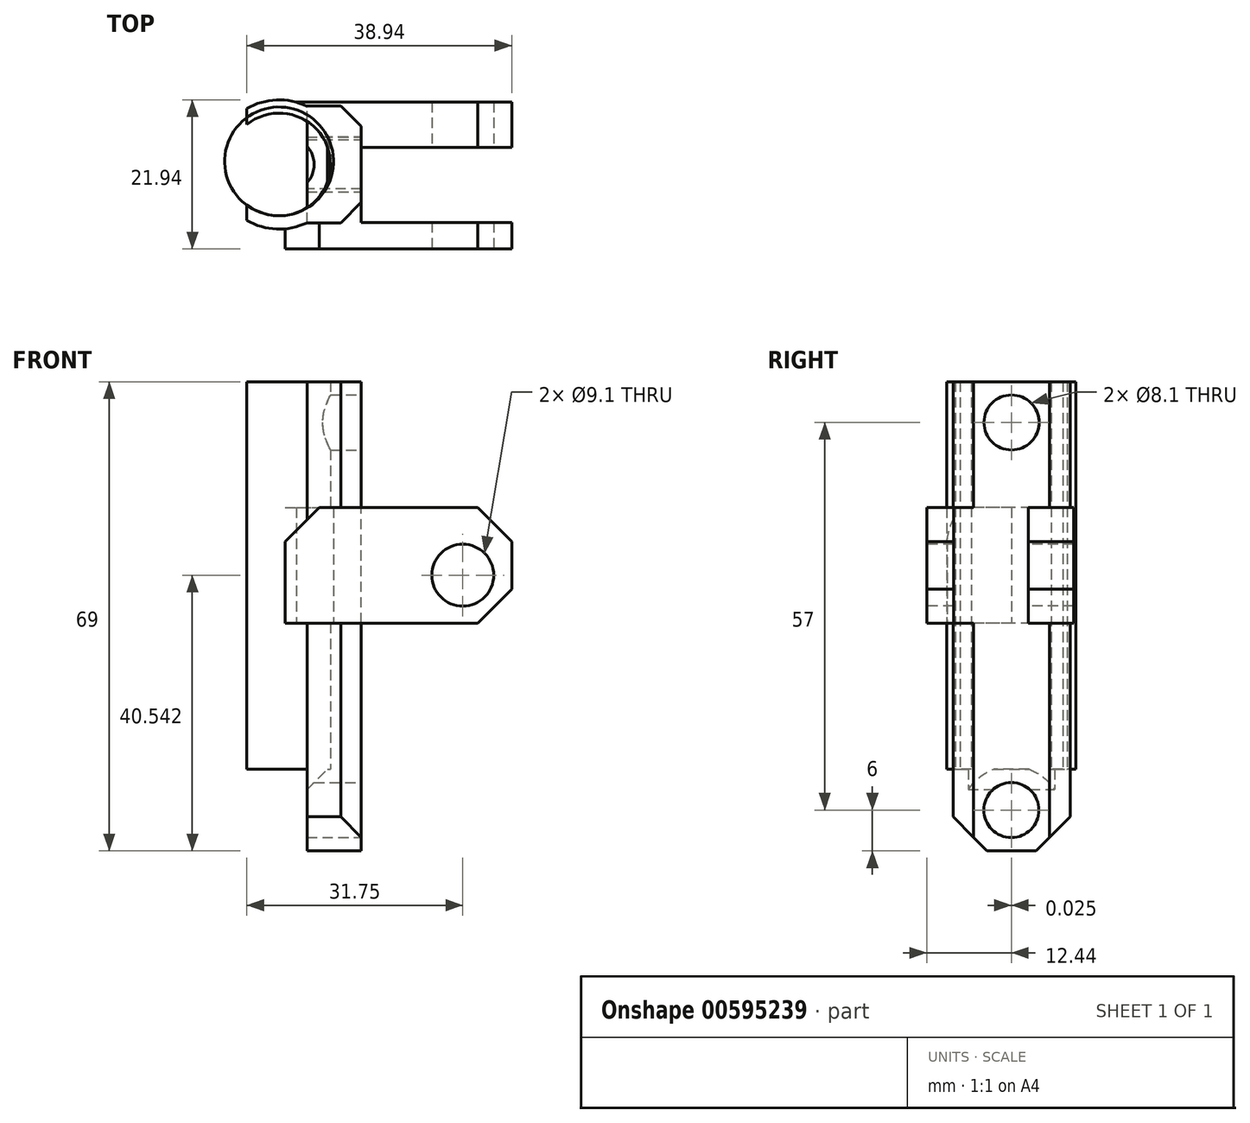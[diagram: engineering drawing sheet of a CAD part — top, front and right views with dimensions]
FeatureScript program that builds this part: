
annotation { "Feature Type Name" : "Feature", "Feature Type Description" : "" }
export const myFeature = defineFeature(function(context is Context, id is Id, definition is map)
    precondition{}
    {
        {
            var Q0;
            Q0=qCreatedBy(makeId("Top.planeOp"),FACE);
            var sketch = newSketch(context, id + "F0", { "sketchPlane" : qUnion([Q0])});
            skCircle(sketch, "E0", {"center": v(0, 0) * mm, "radius": 7.55 * mm});
            skCircle(sketch, "E1", {"center": v(0, 0) * mm, "radius": 9.5 * mm});
            skLineSegment(sketch, "E2", {"start": v(0, 0) * mm, "end": v(-9.5, 0) * mm});
            skLineSegment(sketch, "E3", {"start": v(-9.5, 0) * mm, "end": v(-4.75, 0) * mm});
            skLineSegment(sketch, "E4", {"start": v(-4.75, 0) * mm, "end": v(-4.75, -10.14) * mm});
            skLineSegment(sketch, "E5", {"start": v(-4.75, -10.14) * mm, "end": v(-4.75, 9.64) * mm});
            skCircle(sketch, "E6", {"center": v(0, 0) * mm, "radius": 4.05 * mm});
            skSolve(sketch);
        }
        {
            var Q0;
            {var subQ0=sQuery(id+"F0.wireOp",EDGE,"E5");var subQ1=sQuery(id+"F0.wireOp",EDGE,"E0");var subQ2=makeQuery(id+"F0.imprint","INTERSECT",VERTEX,{"disambiguationData":[OD(0.0)],"derivedFrom":[subQ1,subQ0]});Q0=makeQuery(id+"F0.imprint","IMPRINT",FACE,{"disambiguationData":[TD([[makeQuery(id+"F0.imprint","IMPRINT",EDGE,{"disambiguationData":[TD([[subQ2,1.0]])],"derivedFrom":subQ1}),-1.0]])]});}
            extrude(context, id + "F1", {"entities" : qUnion([Q0]), "depth" : 45 * mm, "offsetDistance" : 25 * mm});
        }
        {
            var Q0;
            Q0=makeQuery(id+"F0.imprint","IMPRINT",FACE,{"disambiguationData":[TD([[makeQuery(id+"F0.imprint","IMPRINT",EDGE,{"derivedFrom":sQuery(id+"F0.wireOp",EDGE,"E6")}),1.0]])]});
            extrude(context, id + "F2", {"entities" : qUnion([Q0]), "depth" : 102.3 * mm, "offsetDistance" : 25 * mm});
        }
        {
            var Q0;
            Q0=makeQuery(id+"F0.imprint","IMPRINT",FACE,{"disambiguationData":[TD([[makeQuery(id+"F0.imprint","IMPRINT",EDGE,{"derivedFrom":sQuery(id+"F0.wireOp",EDGE,"E6")}),1.0]])]});
            extrude(context, id + "F3", {"entities" : qUnion([Q0]), "operationType" : NewBodyOperationType.ADD, "depth" : 25 * mm, "offsetDistance" : 25 * mm});
        }
        {
            var Q0;
            Q0=makeQuery(id+"F0.imprint","IMPRINT",FACE,{"disambiguationData":[TD([[makeQuery(id+"F0.imprint","IMPRINT",EDGE,{"derivedFrom":sQuery(id+"F0.wireOp",EDGE,"E6")}),1.0]])]});
            extrude(context, id + "F4", {"entities" : qUnion([Q0]), "operationType" : NewBodyOperationType.ADD, "oppositeDirection" : true, "depth" : 24.6 * mm, "offsetDistance" : 25 * mm});
        }
        {
            var Q0;
            Q0=makeQuery(id+"F1.opExtrude","CAP_FACE",FACE,{"disambiguationData":[OSD([sQuery(id+"F0.wireOp",EDGE,"E0"),sQuery(id+"F0.wireOp",EDGE,"E1"),sQuery(id+"F0.wireOp",EDGE,"E5")])],"isStart":false});
            var sketch = newSketch(context, id + "F5", { "sketchPlane" : qUnion([Q0])});
            skLineSegment(sketch, "E7", {"start": v(4.09, 0) * mm, "end": v(4.09, -8.58) * mm});
            skLineSegment(sketch, "E8.bottom", {"start": v(4.09, -8.58) * mm, "end": v(12.09, -8.58) * mm});
            skLineSegment(sketch, "E8.top", {"start": v(4.09, 8.62) * mm, "end": v(12.09, 8.62) * mm});
            skLineSegment(sketch, "E8.left", {"start": v(4.09, -8.58) * mm, "end": v(4.09, 8.62) * mm});
            skLineSegment(sketch, "E8.right", {"start": v(12.09, -8.58) * mm, "end": v(12.09, 8.62) * mm});
            skSolve(sketch);
        }
        {
            var Q0;
            {var subQ4=sQuery(id+"F5.wireOp",EDGE,"E8.bottom");Q0=makeQuery(id+"F5.imprint","IMPRINT",FACE,{"disambiguationData":[TD([[makeQuery(id+"F5.imprint","IMPRINT",EDGE,{"derivedFrom":subQ4}),1.0]])]});}
            var Q1;
            {var subQ0=sQuery(id+"F5.wireOp",EDGE,"E8.left");var subQ3=makeQuery(id+"F1.opExtrude","CAP_EDGE",EDGE,{"disambiguationData":[OSD([sQuery(id+"F0.wireOp",EDGE,"E0")])],"isStart":false});var subQ5=makeQuery(id+"F5.imprint","INTERSECT",VERTEX,{"disambiguationData":[OD(1.0)],"derivedFrom":[subQ3,subQ0]});Q1=makeQuery(id+"F5.imprint","IMPRINT",FACE,{"disambiguationData":[TD([[makeQuery(id+"F5.imprint","IMPRINT",EDGE,{"disambiguationData":[TD([[subQ5,-1.0]])],"derivedFrom":subQ0}),-1.0]])]});}
            var Q2;
            {var subQ0=sQuery(id+"F5.wireOp",EDGE,"E8.left");var subQ1=makeQuery(id+"F1.opExtrude","CAP_EDGE",EDGE,{"disambiguationData":[OSD([sQuery(id+"F0.wireOp",EDGE,"E0")])],"isStart":false});var subQ2=makeQuery(id+"F5.imprint","INTERSECT",VERTEX,{"disambiguationData":[OD(0.0)],"derivedFrom":[subQ1,subQ0]});Q2=makeQuery(id+"F5.imprint","IMPRINT",FACE,{"disambiguationData":[TD([[makeQuery(id+"F5.imprint","IMPRINT",EDGE,{"disambiguationData":[TD([[subQ2,-1.0]])],"derivedFrom":subQ0}),-1.0]])]});}
            extrude(context, id + "F6", {"entities" : qUnion([Q0, Q1, Q2]), "operationType" : NewBodyOperationType.ADD, "depth" : 12 * mm, "offsetDistance" : 25 * mm});
        }
        {
            var Q0;
            Q0=makeQuery(id+"F6.opExtrude","SWEPT_FACE",FACE,{"disambiguationData":[OSD([sQuery(id+"F5.wireOp",EDGE,"E8.right")])]});
            var sketch = newSketch(context, id + "F7", { "sketchPlane" : qUnion([Q0])});
            skCircle(sketch, "E9", {"center": v(0.02, 51) * mm, "radius": 4.05 * mm});
            skPoint(sketch, "E9.centerSnap0", {"position": v(-8.58, 51) * mm});
            skPoint(sketch, "E9.centerSnap1", {"position": v(0.02, 57) * mm});
            skSolve(sketch);
        }
        {
            var Q0;
            Q0=makeQuery(id+"F7.imprint","IMPRINT",FACE,{"disambiguationData":[TD([[makeQuery(id+"F7.imprint","IMPRINT",EDGE,{"derivedFrom":sQuery(id+"F7.wireOp",EDGE,"E9")}),1.0]])]});
            extrude(context, id + "F8", {"entities" : qUnion([Q0]), "operationType" : NewBodyOperationType.REMOVE, "oppositeDirection" : true, "depth" : 25 * mm, "offsetDistance" : 25 * mm});
        }
        {
            var Q0;
            {var subQ0=sQuery(id+"F5.wireOp",EDGE,"E8.bottom");var subQ1=sQuery(id+"F5.wireOp",EDGE,"E8.top");var subQ2=sQuery(id+"F0.wireOp",EDGE,"E1");var subQ3=sQuery(id+"F5.wireOp",EDGE,"E8.left");var subQ4=sQuery(id+"F5.wireOp",EDGE,"E8.right");Q0=makeQuery(id+"F6.boolean.opBoolean","SPLIT",FACE,{"disambiguationData":[TD([makeQuery(id+"F1.opExtrude","SWEPT_FACE",FACE,{"disambiguationData":[OSD([subQ2])]})])],"derivedFrom":makeQuery(id+"F6.opExtrude","CAP_FACE",FACE,{"disambiguationData":[OSD([subQ0,subQ1,subQ3,subQ4])],"isStart":true})});}
            extrude(context, id + "F9", {"entities" : qUnion([Q0]), "operationType" : NewBodyOperationType.ADD, "depth" : 45 * mm, "offsetDistance" : 25 * mm});
        }
        {
            var Q0;
            Q0=makeQuery(id+"F9.boolean.opBoolean","MERGE",FACE,{"derivedFrom":[makeQuery(id+"F1.opExtrude","CAP_FACE",FACE,{"disambiguationData":[OSD([sQuery(id+"F0.wireOp",EDGE,"E0"),sQuery(id+"F0.wireOp",EDGE,"E1"),sQuery(id+"F0.wireOp",EDGE,"E5")])],"isStart":true}),makeQuery(id+"F9.opExtrude","CAP_FACE",FACE,{"disambiguationData":[OSD([sQuery(id+"F5.wireOp",EDGE,"E8.bottom"),sQuery(id+"F5.wireOp",EDGE,"E8.top"),sQuery(id+"F5.wireOp",EDGE,"E8.left"),sQuery(id+"F5.wireOp",EDGE,"E8.right")])],"isStart":false})]});
            var sketch = newSketch(context, id + "F10", { "sketchPlane" : qUnion([Q0])});
            skLineSegment(sketch, "E10.bottom", {"start": v(12.09, 8.58) * mm, "end": v(4.09, 8.58) * mm});
            skLineSegment(sketch, "E10.top", {"start": v(12.09, -8.62) * mm, "end": v(4.09, -8.62) * mm});
            skLineSegment(sketch, "E10.left", {"start": v(12.09, 8.58) * mm, "end": v(12.09, -8.62) * mm});
            skLineSegment(sketch, "E10.right", {"start": v(4.09, 8.58) * mm, "end": v(4.09, -8.62) * mm});
            skSolve(sketch);
        }
        {
            var Q0;
            {var subQ1=sQuery(id+"F10.wireOp",EDGE,"E10.bottom");Q0=makeQuery(id+"F10.imprint","IMPRINT",FACE,{"disambiguationData":[TD([[makeQuery(id+"F10.imprint","IMPRINT",EDGE,{"derivedFrom":subQ1}),-1.0]])]});}
            var Q1;
            {var subQ0=sQuery(id+"F10.wireOp",EDGE,"E10.right");var subQ1=makeQuery(id+"F1.opExtrude","CAP_EDGE",EDGE,{"disambiguationData":[OSD([sQuery(id+"F0.wireOp",EDGE,"E0")])],"isStart":true});var subQ2=makeQuery(id+"F10.imprint","INTERSECT",VERTEX,{"disambiguationData":[OD(0.0)],"derivedFrom":[subQ1,subQ0]});Q1=makeQuery(id+"F10.imprint","IMPRINT",FACE,{"disambiguationData":[TD([[makeQuery(id+"F10.imprint","IMPRINT",EDGE,{"disambiguationData":[TD([[subQ2,-1.0]])],"derivedFrom":subQ0}),1.0]])]});}
            extrude(context, id + "F11", {"entities" : qUnion([Q0, Q1]), "operationType" : NewBodyOperationType.ADD, "depth" : 12 * mm, "offsetDistance" : 25 * mm});
        }
        {
            var Q0;
            {var subQ0=sQuery(id+"F5.wireOp",EDGE,"E8.right");Q0=makeQuery(id+"F11.boolean.opBoolean","MERGE",FACE,{"derivedFrom":[makeQuery(id+"F9.boolean.opBoolean","MERGE",FACE,{"derivedFrom":[makeQuery(id+"F6.opExtrude","SWEPT_FACE",FACE,{"disambiguationData":[OSD([subQ0])]}),makeQuery(id+"F9.opExtrude","SWEPT_FACE",FACE,{"disambiguationData":[OSD([subQ0])]})]}),makeQuery(id+"F11.opExtrude","SWEPT_FACE",FACE,{"disambiguationData":[OSD([sQuery(id+"F10.wireOp",EDGE,"E10.left")])]})]});}
            var sketch = newSketch(context, id + "F12", { "sketchPlane" : qUnion([Q0])});
            skLineSegment(sketch, "E11", {"start": v(-8.58, -12) * mm, "end": v(-8.58, 0) * mm});
            skLineSegment(sketch, "E12", {"start": v(-8.58, 0) * mm, "end": v(8.62, 0) * mm});
            skCircle(sketch, "E13", {"center": v(0, -6) * mm, "radius": 4.05 * mm});
            skPoint(sketch, "E13.centerSnap0", {"position": v(-8.58, -6) * mm});
            skSolve(sketch);
        }
        {
            var Q0;
            Q0=makeQuery(id+"F12.imprint","IMPRINT",FACE,{"disambiguationData":[TD([[makeQuery(id+"F12.imprint","IMPRINT",EDGE,{"derivedFrom":sQuery(id+"F12.wireOp",EDGE,"E13")}),1.0]])]});
            extrude(context, id + "F13", {"entities" : qUnion([Q0]), "operationType" : NewBodyOperationType.REMOVE, "oppositeDirection" : true, "depth" : 25 * mm, "offsetDistance" : 25 * mm});
        }
        {
            var Q0;
            {var subQ0=sQuery(id+"F0.wireOp",EDGE,"E5");var subQ1=sQuery(id+"F0.wireOp",EDGE,"E1");var subQ2=sQuery(id+"F0.wireOp",EDGE,"E0");var subQ3=sQuery(id+"F5.wireOp",EDGE,"E8.bottom");Q0=makeQuery(id+"F6.boolean.opBoolean","SPLIT",FACE,{"disambiguationData":[TD([makeQuery(id+"F6.opExtrude","SWEPT_FACE",FACE,{"disambiguationData":[OSD([subQ3])]})])],"derivedFrom":makeQuery(id+"F1.opExtrude","CAP_FACE",FACE,{"disambiguationData":[OSD([subQ2,subQ1,subQ0])],"isStart":false})});}
            var Q1;
            {var subQ1=sQuery(id+"F0.wireOp",EDGE,"E1");var subQ2=sQuery(id+"F0.wireOp",EDGE,"E5");var subQ3=sQuery(id+"F0.wireOp",EDGE,"E0");Q1=makeQuery(id+"F6.boolean.opBoolean","SPLIT",FACE,{"disambiguationData":[TD([makeQuery(id+"F1.opExtrude","SWEPT_FACE",FACE,{"disambiguationData":[OSD([subQ2]),TDD([makeQuery(id+"F0.imprint","IMPRINT",EDGE,{"disambiguationData":[TD([[makeQuery(id+"F0.imprint","INTERSECT",VERTEX,{"disambiguationData":[OD(0.0)],"derivedFrom":[subQ1,subQ2]}),1.0]])],"derivedFrom":subQ2})])]})])],"derivedFrom":makeQuery(id+"F1.opExtrude","CAP_FACE",FACE,{"disambiguationData":[OSD([subQ3,subQ1,subQ2])],"isStart":false})});}
            extrude(context, id + "F14", {"entities" : qUnion([Q0, Q1]), "operationType" : NewBodyOperationType.ADD, "depth" : 12 * mm, "offsetDistance" : 25 * mm});
        }
        {
            var Q0;
            Q0=makeQuery(id+"F11.opExtrude","CAP_EDGE",EDGE,{"disambiguationData":[OSD([sQuery(id+"F10.wireOp",EDGE,"E10.top")])],"isStart":false});
            var Q1;
            Q1=makeQuery(id+"F11.opExtrude","CAP_EDGE",EDGE,{"disambiguationData":[OSD([sQuery(id+"F10.wireOp",EDGE,"E10.bottom")])],"isStart":false});
            chamfer(context, id + "F15", {"entities" : qUnion([Q0, Q1]), "width" : 5 * mm, "tangentPropagation" : true});
        }
        {
            var Q0;
            {var subQ0=sQuery(id+"F5.wireOp",EDGE,"E8.right");var subQ1=sQuery(id+"F5.wireOp",EDGE,"E8.top");Q0=makeQuery(id+"F11.boolean.opBoolean","MERGE",EDGE,{"derivedFrom":[makeQuery(id+"F9.boolean.opBoolean","MERGE",EDGE,{"derivedFrom":[makeQuery(id+"F6.opExtrude","SWEPT_EDGE",EDGE,{"disambiguationData":[OSD([subQ1,subQ0])]}),makeQuery(id+"F9.opExtrude","SWEPT_EDGE",EDGE,{"disambiguationData":[OSD([subQ1,subQ0])]})]}),makeQuery(id+"F11.opExtrude","SWEPT_EDGE",EDGE,{"disambiguationData":[OSD([sQuery(id+"F10.wireOp",EDGE,"E10.top"),sQuery(id+"F10.wireOp",EDGE,"E10.left")])]})]});}
            var Q1;
            {var subQ0=sQuery(id+"F5.wireOp",EDGE,"E8.right");var subQ1=sQuery(id+"F5.wireOp",EDGE,"E8.bottom");Q1=makeQuery(id+"F11.boolean.opBoolean","MERGE",EDGE,{"derivedFrom":[makeQuery(id+"F9.boolean.opBoolean","MERGE",EDGE,{"derivedFrom":[makeQuery(id+"F6.opExtrude","SWEPT_EDGE",EDGE,{"disambiguationData":[OSD([subQ1,subQ0])]}),makeQuery(id+"F9.opExtrude","SWEPT_EDGE",EDGE,{"disambiguationData":[OSD([subQ1,subQ0])]})]}),makeQuery(id+"F11.opExtrude","SWEPT_EDGE",EDGE,{"disambiguationData":[OSD([sQuery(id+"F10.wireOp",EDGE,"E10.bottom"),sQuery(id+"F10.wireOp",EDGE,"E10.left")])]})]});}
            chamfer(context, id + "F16", {"entities" : qUnion([Q0, Q1]), "width" : 3 * mm, "tangentPropagation" : true});
        }
        {
            var Q0;
            Q0=makeQuery(id+"F4.opExtrude","CAP_FACE",FACE,{"disambiguationData":[OSD([sQuery(id+"F0.wireOp",EDGE,"E6")])],"isStart":false});
            extrude(context, id + "F17", {"entities" : qUnion([Q0]), "operationType" : NewBodyOperationType.REMOVE, "oppositeDirection" : true, "depth" : 164 * mm, "offsetDistance" : 25 * mm});
        }
        {
            var Q0;
            {var subQ0=sQuery(id+"F5.wireOp",EDGE,"E8.left");var subQ1=sQuery(id+"F10.wireOp",EDGE,"E10.right");Q0=makeQuery(id+"F11.boolean.opBoolean","SPLIT",EDGE,{"disambiguationData":[topologyDisambiguationEdgeConnected([makeQuery(id+"F6.opExtrude","SWEPT_FACE",FACE,{"disambiguationData":[OSD([subQ0])]}),makeQuery(id+"F9.opExtrude","SWEPT_FACE",FACE,{"disambiguationData":[OSD([subQ0])]}),makeQuery(id+"F11.opExtrude","CAP_FACE",FACE,{"disambiguationData":[OSD([sQuery(id+"F10.wireOp",EDGE,"E10.bottom"),sQuery(id+"F10.wireOp",EDGE,"E10.top"),sQuery(id+"F10.wireOp",EDGE,"E10.left"),subQ1])],"isStart":true}),makeQuery(id+"F11.opExtrude","SWEPT_FACE",FACE,{"disambiguationData":[OSD([subQ1])]})])],"derivedFrom":makeQuery(id+"F11.opExtrude","CAP_EDGE",EDGE,{"disambiguationData":[OSD([subQ1])],"isStart":true})});}
            chamfer(context, id + "F18", {"entities" : qUnion([Q0]), "width" : 3 * mm, "tangentPropagation" : true});
        }
        {
            var Q0;
            {var subQ0=sQuery(id+"F5.wireOp",EDGE,"E8.right");Q0=makeQuery(id+"F11.boolean.opBoolean","MERGE",FACE,{"derivedFrom":[makeQuery(id+"F9.boolean.opBoolean","MERGE",FACE,{"derivedFrom":[makeQuery(id+"F6.opExtrude","SWEPT_FACE",FACE,{"disambiguationData":[OSD([subQ0])]}),makeQuery(id+"F9.opExtrude","SWEPT_FACE",FACE,{"disambiguationData":[OSD([subQ0])]})]}),makeQuery(id+"F11.opExtrude","SWEPT_FACE",FACE,{"disambiguationData":[OSD([sQuery(id+"F10.wireOp",EDGE,"E10.left")])]})]});}
            var sketch = newSketch(context, id + "F19", { "sketchPlane" : qUnion([Q0])});
            skLineSegment(sketch, "E14", {"start": v(0, -10.05) * mm, "end": v(0, -1.95) * mm});
            skLineSegment(sketch, "E15", {"start": v(0, -1.95) * mm, "end": v(0, -6) * mm});
            skLineSegment(sketch, "E16", {"start": v(0, -6) * mm, "end": v(-4.87, -6) * mm});
            skLineSegment(sketch, "E17", {"start": v(0, 46.95) * mm, "end": v(0, 55.05) * mm});
            skLineSegment(sketch, "E18", {"start": v(0, 55.05) * mm, "end": v(0.02, 51) * mm});
            skLineSegment(sketch, "E19", {"start": v(0.02, 51) * mm, "end": v(-4.92, 50.97) * mm});
            skLineSegment(sketch, "E20", {"start": v(-2.44, -6) * mm, "end": v(-2.44, 50.98) * mm});
            skLineSegment(sketch, "E21", {"start": v(-2.44, -6) * mm, "end": v(-2.44, 22.5) * mm});
            skLineSegment(sketch, "E22", {"start": v(-2.44, 22.5) * mm, "end": v(-2.44, 15.5) * mm});
            skLineSegment(sketch, "E23.bottom", {"start": v(-2.44, 15.5) * mm, "end": v(-12.44, 15.5) * mm});
            skLineSegment(sketch, "E23.top", {"start": v(-2.44, 22.5) * mm, "end": v(-12.44, 22.5) * mm});
            skLineSegment(sketch, "E23.left", {"start": v(-2.44, 15.5) * mm, "end": v(-2.44, 22.5) * mm});
            skLineSegment(sketch, "E23.right", {"start": v(-12.44, 15.5) * mm, "end": v(-12.44, 22.5) * mm});
            skLineSegment(sketch, "E24", {"start": v(-8.44, 15.5) * mm, "end": v(-8.44, 22.5) * mm});
            skSolve(sketch);
        }
        {
            var Q0;
            {var subQ0=sQuery(id+"F19.wireOp",EDGE,"E23.right");Q0=makeQuery(id+"F19.imprint","IMPRINT",FACE,{"disambiguationData":[TD([[makeQuery(id+"F19.imprint","IMPRINT",EDGE,{"derivedFrom":subQ0}),-1.0]])]});}
            extrude(context, id + "F20", {"entities" : qUnion([Q0]), "operationType" : NewBodyOperationType.ADD, "oppositeDirection" : true, "depth" : 11.2 * mm, "offsetDistance" : 25 * mm});
        }
        {
            var Q0;
            {var subQ0=sQuery(id+"F19.wireOp",EDGE,"E23.right");Q0=makeQuery(id+"F19.imprint","IMPRINT",FACE,{"disambiguationData":[TD([[makeQuery(id+"F19.imprint","IMPRINT",EDGE,{"derivedFrom":subQ0}),-1.0]])]});}
            extrude(context, id + "F21", {"entities" : qUnion([Q0]), "operationType" : NewBodyOperationType.ADD, "depth" : 40 * mm, "offsetDistance" : 25 * mm});
        }
        {
            var Q0;
            {var subQ0=sQuery(id+"F19.wireOp",EDGE,"E23.right");Q0=makeQuery(id+"F21.boolean.opBoolean","MERGE",FACE,{"derivedFrom":[makeQuery(id+"F20.opExtrude","SWEPT_FACE",FACE,{"disambiguationData":[OSD([subQ0])]}),makeQuery(id+"F21.opExtrude","SWEPT_FACE",FACE,{"disambiguationData":[OSD([subQ0])]})]});}
            var sketch = newSketch(context, id + "F22", { "sketchPlane" : qUnion([Q0])});
            skLineSegment(sketch, "E25", {"start": v(4.09, 15.5) * mm, "end": v(-4.75, 15.5) * mm});
            skLineSegment(sketch, "E26", {"start": v(-4.75, 15.5) * mm, "end": v(-0.33, 15.5) * mm});
            skLineSegment(sketch, "E27", {"start": v(2.22, 15.5) * mm, "end": v(2.22, 22.5) * mm});
            skLineSegment(sketch, "E28", {"start": v(2.22, 22.5) * mm, "end": v(2.22, 19) * mm});
            skLineSegment(sketch, "E29", {"start": v(0, 19) * mm, "end": v(27, 19) * mm});
            skCircle(sketch, "E30", {"center": v(27, 28.54) * mm, "radius": 4.55 * mm});
            skSolve(sketch);
        }
        {
            var Q0;
            {var subQ0=sQuery(id+"F19.wireOp",EDGE,"E23.top");Q0=makeQuery(id+"F21.boolean.opBoolean","MERGE",FACE,{"derivedFrom":[makeQuery(id+"F20.opExtrude","SWEPT_FACE",FACE,{"disambiguationData":[OSD([subQ0])]}),makeQuery(id+"F21.opExtrude","SWEPT_FACE",FACE,{"disambiguationData":[OSD([subQ0])]})]});}
            extrude(context, id + "F23", {"entities" : qUnion([Q0]), "operationType" : NewBodyOperationType.ADD, "depth" : 16 * mm, "offsetDistance" : 25 * mm});
        }
        {
            var Q0;
            {var subQ0=sQuery(id+"F19.wireOp",EDGE,"E23.top");var subQ1=sQuery(id+"F19.wireOp",EDGE,"E23.bottom");Q0=makeQuery(id+"F23.boolean.opBoolean","MERGE",FACE,{"derivedFrom":[makeQuery(id+"FqEzdGLLWJqbQr5_1.boolean.opBoolean","MERGE",FACE,{"derivedFrom":[makeQuery(id+"F21.opExtrude","CAP_FACE",FACE,{"disambiguationData":[OSD([subQ1,subQ0,sQuery(id+"F19.wireOp",EDGE,"E23.right"),sQuery(id+"F19.wireOp",EDGE,"E24")])],"isStart":false}),makeQuery(id+"FqEzdGLLWJqbQr5_1.opExtrude","SWEPT_FACE",FACE,{"disambiguationData":[OSD([subQ1]),TDD([makeQuery(id+"F21.opExtrude","CAP_EDGE",EDGE,{"disambiguationData":[OSD([subQ1])],"isStart":false})])]})]}),makeQuery(id+"F23.opExtrude","SWEPT_FACE",FACE,{"disambiguationData":[OSD([subQ0]),TDD([makeQuery(id+"F21.opExtrude","CAP_EDGE",EDGE,{"disambiguationData":[OSD([subQ0])],"isStart":false})])]})]});}
            extrude(context, id + "F24", {"entities" : qUnion([Q0]), "operationType" : NewBodyOperationType.REMOVE, "oppositeDirection" : true, "depth" : 17.9 * mm, "offsetDistance" : 25 * mm});
        }
        {
            var Q0;
            {var subQ0=sQuery(id+"F22.wireOp",EDGE,"E30");var subQ9=makeQuery(id+"F22.imprint","INTERSECT",VERTEX,{"derivedFrom":[sQuery(id+"F22.wireOp",EDGE,"E29"),subQ0]});Q0=makeQuery(id+"F22.imprint","IMPRINT",FACE,{"disambiguationData":[TD([[makeQuery(id+"F22.imprint","IMPRINT",EDGE,{"disambiguationData":[TD([[subQ9,1.0]])],"derivedFrom":subQ0}),1.0]])]});}
            var Q1;
            {var subQ0=sQuery(id+"F22.wireOp",EDGE,"E30");var subQ1=sQuery(id+"F19.wireOp",EDGE,"E23.right");var subQ2=sQuery(id+"F19.wireOp",EDGE,"E23.bottom");var subQ3=makeQuery(id+"F21.boolean.opBoolean","MERGE",EDGE,{"derivedFrom":[makeQuery(id+"F20.opExtrude","SWEPT_EDGE",EDGE,{"disambiguationData":[OSD([subQ2,subQ1])]}),makeQuery(id+"F21.opExtrude","SWEPT_EDGE",EDGE,{"disambiguationData":[OSD([subQ2,subQ1])]})]});var subQ4=makeQuery(id+"F22.imprint","INTERSECT",VERTEX,{"disambiguationData":[OD(0.0)],"derivedFrom":[subQ3,subQ0]});Q1=makeQuery(id+"F22.imprint","IMPRINT",FACE,{"disambiguationData":[TD([[makeQuery(id+"F22.imprint","IMPRINT",EDGE,{"disambiguationData":[TD([[subQ4,-1.0]])],"derivedFrom":subQ0}),1.0]])]});}
            var Q2;
            {var subQ0=sQuery(id+"F22.wireOp",EDGE,"E30");var subQ1=sQuery(id+"F19.wireOp",EDGE,"E23.right");var subQ2=sQuery(id+"F19.wireOp",EDGE,"E23.top");var subQ3=makeQuery(id+"F21.boolean.opBoolean","MERGE",EDGE,{"derivedFrom":[makeQuery(id+"F20.opExtrude","SWEPT_EDGE",EDGE,{"disambiguationData":[OSD([subQ2,subQ1])]}),makeQuery(id+"F21.opExtrude","SWEPT_EDGE",EDGE,{"disambiguationData":[OSD([subQ2,subQ1])]})]});var subQ4=makeQuery(id+"F22.imprint","INTERSECT",VERTEX,{"disambiguationData":[OD(0.0)],"derivedFrom":[subQ3,subQ0]});Q2=makeQuery(id+"F22.imprint","IMPRINT",FACE,{"disambiguationData":[TD([[makeQuery(id+"F22.imprint","IMPRINT",EDGE,{"disambiguationData":[TD([[subQ4,1.0]])],"derivedFrom":subQ0}),1.0]])]});}
            extrude(context, id + "F25", {"entities" : qUnion([Q0, Q1, Q2]), "operationType" : NewBodyOperationType.REMOVE, "oppositeDirection" : true, "depth" : 25 * mm, "offsetDistance" : 25 * mm});
        }
        {
            var Q0;
            {var subQ0=sQuery(id+"F19.wireOp",EDGE,"E23.bottom");Q0=makeQuery(id+"F21.boolean.opBoolean","MERGE",FACE,{"derivedFrom":[makeQuery(id+"F20.opExtrude","SWEPT_FACE",FACE,{"disambiguationData":[OSD([subQ0])]}),makeQuery(id+"F21.opExtrude","SWEPT_FACE",FACE,{"disambiguationData":[OSD([subQ0])]})]});}
            extrude(context, id + "F26", {"entities" : qUnion([Q0]), "operationType" : NewBodyOperationType.REMOVE, "oppositeDirection" : true, "depth" : 6 * mm, "offsetDistance" : 25 * mm});
        }
        {
            var Q0;
            {var subQ0=sQuery(id+"F19.wireOp",EDGE,"E23.right");Q0=makeQuery(id+"F23.boolean.opBoolean","MERGE",FACE,{"derivedFrom":[makeQuery(id+"F21.boolean.opBoolean","MERGE",FACE,{"derivedFrom":[makeQuery(id+"F20.opExtrude","SWEPT_FACE",FACE,{"disambiguationData":[OSD([subQ0])]}),makeQuery(id+"F21.opExtrude","SWEPT_FACE",FACE,{"disambiguationData":[OSD([subQ0])]})]}),makeQuery(id+"F23.opExtrude","SWEPT_FACE",FACE,{"disambiguationData":[OSD([sQuery(id+"F19.wireOp",EDGE,"E23.top"),subQ0])]})]});}
            extrude(context, id + "F27", {"entities" : qUnion([Q0]), "operationType" : NewBodyOperationType.ADD, "oppositeDirection" : true, "depth" : 21.6 * mm, "offsetDistance" : 25 * mm});
        }
        {
            var Q0;
            {var subQ0=sQuery(id+"F19.wireOp",EDGE,"E23.right");var subQ1=sQuery(id+"F19.wireOp",EDGE,"E23.top");Q0=makeQuery(id+"F27.boolean.opBoolean","MERGE",FACE,{"derivedFrom":[makeQuery(id+"F24.boolean.opBoolean","COPY",FACE,{"derivedFrom":makeQuery(id+"F24.opExtrude","CAP_FACE",FACE,{"disambiguationData":[OSD([sQuery(id+"F19.wireOp",EDGE,"E23.bottom"),subQ1,subQ0,sQuery(id+"F19.wireOp",EDGE,"E24")])],"isStart":false})}),makeQuery(id+"F27.opExtrude","SWEPT_FACE",FACE,{"disambiguationData":[OSD([subQ1,subQ0]),TDD([makeQuery(id+"F24.boolean.opBoolean","COPY",EDGE,{"derivedFrom":makeQuery(id+"F24.opExtrude","CAP_EDGE",EDGE,{"disambiguationData":[OSD([subQ1,subQ0])],"isStart":false})})])]})]});}
            var sketch = newSketch(context, id + "F28", { "sketchPlane" : qUnion([Q0])});
            skLineSegment(sketch, "E31.bottom", {"start": v(-8.51, 21.5) * mm, "end": v(0.49, 21.5) * mm});
            skLineSegment(sketch, "E31.top", {"start": v(-8.51, 38.5) * mm, "end": v(0.49, 38.5) * mm});
            skLineSegment(sketch, "E31.left", {"start": v(-8.51, 21.5) * mm, "end": v(-8.51, 38.5) * mm});
            skLineSegment(sketch, "E31.right", {"start": v(0.49, 21.5) * mm, "end": v(0.49, 38.5) * mm});
            skPoint(sketch, "E31.middle", {"position": v(-3.6, 29.62) * mm});
            skPoint(sketch, "E31.middle.positionSnap0", {"position": v(-12.44, 30) * mm});
            skPoint(sketch, "E31.middle.positionSnap1", {"position": v(-1.64, 21.5) * mm});
            skPoint(sketch, "E31.centerSnap0", {"position": v(-12.44, 30) * mm});
            skPoint(sketch, "E31.centerSnap1", {"position": v(-1.64, 21.5) * mm});
            skSolve(sketch);
        }
        {
            var Q0;
            Q0=makeQuery(id+"F28.imprint","IMPRINT",FACE,{"disambiguationData":[TD([[makeQuery(id+"F28.imprint","IMPRINT",EDGE,{"derivedFrom":sQuery(id+"F28.wireOp",EDGE,"E31.bottom")}),-1.0]])]});
            extrude(context, id + "F29", {"entities" : qUnion([Q0]), "operationType" : NewBodyOperationType.REMOVE, "oppositeDirection" : true, "depth" : 22.1 * mm, "offsetDistance" : 25 * mm});
        }
        {
            var Q0;
            Q0=makeQuery(id+"F29.boolean.opBoolean","COPY",FACE,{"derivedFrom":makeQuery(id+"F29.opExtrude","SWEPT_FACE",FACE,{"disambiguationData":[OSD([sQuery(id+"F28.wireOp",EDGE,"E31.right")])]})});
            extrude(context, id + "F30", {"entities" : qUnion([Q0]), "operationType" : NewBodyOperationType.REMOVE, "oppositeDirection" : true, "depth" : 2 * mm, "offsetDistance" : 25 * mm});
        }
        {
            var Q0;
            {var subQ0=sQuery(id+"F19.wireOp",EDGE,"E23.right");var subQ2=sQuery(id+"F19.wireOp",EDGE,"E23.bottom");Q0=makeQuery(id+"F29.boolean.opBoolean","SPLIT",EDGE,{"disambiguationData":[TD([makeQuery(id+"F29.opExtrude","SWEPT_FACE",FACE,{"disambiguationData":[OSD([sQuery(id+"F28.wireOp",EDGE,"E31.right")])]})])],"derivedFrom":makeQuery(id+"F27.boolean.opBoolean","MERGE",EDGE,{"derivedFrom":[makeQuery(id+"F26.boolean.opBoolean","COPY",EDGE,{"derivedFrom":makeQuery(id+"F26.opExtrude","CAP_EDGE",EDGE,{"disambiguationData":[OSD([subQ2]),TDD([makeQuery(id+"F24.boolean.opBoolean","COPY",EDGE,{"derivedFrom":makeQuery(id+"F24.opExtrude","CAP_EDGE",EDGE,{"disambiguationData":[OSD([subQ2])],"isStart":false})})])],"isStart":false})}),makeQuery(id+"F27.opExtrude","SWEPT_EDGE",EDGE,{"disambiguationData":[OSD([subQ2,subQ0]),TDD([makeQuery(id+"F26.boolean.opBoolean","COPY",VERTEX,{"derivedFrom":makeQuery(id+"F26.opExtrude","CAP_VERTEX",VERTEX,{"disambiguationData":[OSD([subQ2,subQ0]),TDD([makeQuery(id+"F24.boolean.opBoolean","COPY",VERTEX,{"derivedFrom":makeQuery(id+"F24.opExtrude","CAP_VERTEX",VERTEX,{"disambiguationData":[OSD([subQ2,subQ0])],"isStart":false})})])],"isStart":false})})])]})]})});}
            var Q1;
            {var subQ0=sQuery(id+"F19.wireOp",EDGE,"E23.right");var subQ1=sQuery(id+"F19.wireOp",EDGE,"E23.top");Q1=makeQuery(id+"F29.boolean.opBoolean","SPLIT",EDGE,{"disambiguationData":[TD([makeQuery(id+"F29.opExtrude","SWEPT_FACE",FACE,{"disambiguationData":[OSD([sQuery(id+"F28.wireOp",EDGE,"E31.right")])]})])],"derivedFrom":makeQuery(id+"F27.boolean.opBoolean","MERGE",EDGE,{"derivedFrom":[makeQuery(id+"F24.boolean.opBoolean","COPY",EDGE,{"derivedFrom":makeQuery(id+"F24.opExtrude","CAP_EDGE",EDGE,{"disambiguationData":[OSD([subQ1])],"isStart":false})}),makeQuery(id+"F27.opExtrude","SWEPT_EDGE",EDGE,{"disambiguationData":[OSD([subQ1,subQ0]),TDD([makeQuery(id+"F24.boolean.opBoolean","COPY",VERTEX,{"derivedFrom":makeQuery(id+"F24.opExtrude","CAP_VERTEX",VERTEX,{"disambiguationData":[OSD([subQ1,subQ0])],"isStart":false})})])]})]})});}
            var Q2;
            {var subQ0=sQuery(id+"F19.wireOp",EDGE,"E23.right");var subQ2=sQuery(id+"F19.wireOp",EDGE,"E23.bottom");Q2=makeQuery(id+"F29.boolean.opBoolean","SPLIT",EDGE,{"disambiguationData":[TD([makeQuery(id+"F20.opExtrude","SWEPT_FACE",FACE,{"disambiguationData":[OSD([subQ0])]})])],"derivedFrom":makeQuery(id+"F27.boolean.opBoolean","MERGE",EDGE,{"derivedFrom":[makeQuery(id+"F26.boolean.opBoolean","COPY",EDGE,{"derivedFrom":makeQuery(id+"F26.opExtrude","CAP_EDGE",EDGE,{"disambiguationData":[OSD([subQ2]),TDD([makeQuery(id+"F24.boolean.opBoolean","COPY",EDGE,{"derivedFrom":makeQuery(id+"F24.opExtrude","CAP_EDGE",EDGE,{"disambiguationData":[OSD([subQ2])],"isStart":false})})])],"isStart":false})}),makeQuery(id+"F27.opExtrude","SWEPT_EDGE",EDGE,{"disambiguationData":[OSD([subQ2,subQ0]),TDD([makeQuery(id+"F26.boolean.opBoolean","COPY",VERTEX,{"derivedFrom":makeQuery(id+"F26.opExtrude","CAP_VERTEX",VERTEX,{"disambiguationData":[OSD([subQ2,subQ0]),TDD([makeQuery(id+"F24.boolean.opBoolean","COPY",VERTEX,{"derivedFrom":makeQuery(id+"F24.opExtrude","CAP_VERTEX",VERTEX,{"disambiguationData":[OSD([subQ2,subQ0])],"isStart":false})})])],"isStart":false})})])]})]})});}
            var Q3;
            {var subQ0=sQuery(id+"F19.wireOp",EDGE,"E23.right");var subQ1=sQuery(id+"F19.wireOp",EDGE,"E23.top");Q3=makeQuery(id+"F29.boolean.opBoolean","SPLIT",EDGE,{"disambiguationData":[TD([makeQuery(id+"F20.opExtrude","SWEPT_FACE",FACE,{"disambiguationData":[OSD([subQ0])]})])],"derivedFrom":makeQuery(id+"F27.boolean.opBoolean","MERGE",EDGE,{"derivedFrom":[makeQuery(id+"F24.boolean.opBoolean","COPY",EDGE,{"derivedFrom":makeQuery(id+"F24.opExtrude","CAP_EDGE",EDGE,{"disambiguationData":[OSD([subQ1])],"isStart":false})}),makeQuery(id+"F27.opExtrude","SWEPT_EDGE",EDGE,{"disambiguationData":[OSD([subQ1,subQ0]),TDD([makeQuery(id+"F24.boolean.opBoolean","COPY",VERTEX,{"derivedFrom":makeQuery(id+"F24.opExtrude","CAP_VERTEX",VERTEX,{"disambiguationData":[OSD([subQ1,subQ0])],"isStart":false})})])]})]})});}
            var Q4;
            {var subQ0=sQuery(id+"F19.wireOp",EDGE,"E23.top");Q4=makeQuery(id+"F23.opExtrude","CAP_EDGE",EDGE,{"disambiguationData":[OSD([subQ0]),TDD([makeQuery(id+"F20.opExtrude","CAP_EDGE",EDGE,{"disambiguationData":[OSD([subQ0])],"isStart":false})])],"isStart":false});}
            var Q5;
            {var subQ0=sQuery(id+"F19.wireOp",EDGE,"E23.bottom");Q5=makeQuery(id+"F26.boolean.opBoolean","COPY",EDGE,{"derivedFrom":makeQuery(id+"F26.opExtrude","CAP_EDGE",EDGE,{"disambiguationData":[OSD([subQ0]),TDD([makeQuery(id+"F20.opExtrude","CAP_EDGE",EDGE,{"disambiguationData":[OSD([subQ0])],"isStart":false})])],"isStart":false})});}
            chamfer(context, id + "F31", {"entities" : qUnion([Q0, Q1, Q2, Q3, Q4, Q5]), "width" : 5 * mm, "tangentPropagation" : true});
        }
        {
            var Q0;
            {var subQ0=sQuery(id+"F19.wireOp",EDGE,"E23.right");var subQ1=sQuery(id+"F19.wireOp",EDGE,"E23.top");Q0=makeQuery(id+"F27.opExtrude","SWEPT_FACE",FACE,{"disambiguationData":[OSD([subQ1,subQ0]),TDD([makeQuery(id+"F23.boolean.opBoolean","MERGE",EDGE,{"derivedFrom":[makeQuery(id+"F20.opExtrude","CAP_EDGE",EDGE,{"disambiguationData":[OSD([subQ0])],"isStart":false}),makeQuery(id+"F23.opExtrude","SWEPT_EDGE",EDGE,{"disambiguationData":[OSD([subQ1,subQ0]),TDD([makeQuery(id+"F20.opExtrude","CAP_VERTEX",VERTEX,{"disambiguationData":[OSD([subQ1,subQ0])],"isStart":false})])]})]})])]});}
            extrude(context, id + "F32", {"entities" : qUnion([Q0]), "operationType" : NewBodyOperationType.REMOVE, "oppositeDirection" : true, "depth" : 7.1 * mm, "offsetDistance" : 25 * mm});
        }
        {
            var Q0;
            {var subQ0=sQuery(id+"F19.wireOp",EDGE,"E23.right");var subQ1=sQuery(id+"F19.wireOp",EDGE,"E23.top");var subQ4=sQuery(id+"F0.wireOp",EDGE,"E5");var subQ5=sQuery(id+"F0.wireOp",EDGE,"E1");var subQ6=sQuery(id+"F0.wireOp",EDGE,"E0");var subQ7=makeQuery(id+"F1.opExtrude","CAP_FACE",FACE,{"disambiguationData":[OSD([subQ6,subQ5,subQ4])],"isStart":false});var subQ8=makeQuery(id+"F1.opExtrude","SWEPT_FACE",FACE,{"disambiguationData":[OSD([subQ6])]});var subQ10=makeQuery(id+"F1.opExtrude","CAP_EDGE",EDGE,{"disambiguationData":[OSD([subQ6])],"isStart":false});Q0=makeQuery(id+"F32.boolean.opBoolean","COPY",EDGE,{"derivedFrom":makeQuery(id+"F32.opExtrude","CAP_EDGE",EDGE,{"disambiguationData":[OSD([subQ6,subQ1,subQ0]),TDD([makeQuery(id+"F27.boolean.opBoolean","INTERSECT",EDGE,{"disambiguationData":[OD(1.0)],"derivedFrom":[makeQuery(id+"F14.boolean.opBoolean","MERGE",FACE,{"derivedFrom":[subQ8,makeQuery(id+"F14.opExtrude","SWEPT_FACE",FACE,{"disambiguationData":[OSD([subQ6]),TDD([makeQuery(id+"F6.boolean.opBoolean","SPLIT",EDGE,{"disambiguationData":[topologyDisambiguationEdgeConnected([subQ8,subQ7]),TD([makeQuery(id+"F1.opExtrude","SWEPT_FACE",FACE,{"disambiguationData":[OSD([subQ4]),TDD([makeQuery(id+"F0.imprint","IMPRINT",EDGE,{"disambiguationData":[TD([[makeQuery(id+"F0.imprint","INTERSECT",VERTEX,{"disambiguationData":[OD(0.0)],"derivedFrom":[subQ5,subQ4]}),1.0]])],"derivedFrom":subQ4})])]})])],"derivedFrom":subQ10})])]}),makeQuery(id+"F14.opExtrude","SWEPT_FACE",FACE,{"disambiguationData":[OSD([subQ6]),TDD([makeQuery(id+"F6.boolean.opBoolean","SPLIT",EDGE,{"disambiguationData":[topologyDisambiguationEdgeConnected([subQ8,subQ7]),TD([makeQuery(id+"F1.opExtrude","SWEPT_FACE",FACE,{"disambiguationData":[OSD([subQ4]),TDD([makeQuery(id+"F0.imprint","IMPRINT",EDGE,{"disambiguationData":[TD([[makeQuery(id+"F0.imprint","INTERSECT",VERTEX,{"disambiguationData":[OD(1.0)],"derivedFrom":[subQ5,subQ4]}),-1.0]])],"derivedFrom":subQ4})])]})])],"derivedFrom":subQ10})])]})]}),makeQuery(id+"F27.opExtrude","SWEPT_FACE",FACE,{"disambiguationData":[OSD([subQ1,subQ0]),TDD([makeQuery(id+"F23.boolean.opBoolean","MERGE",EDGE,{"derivedFrom":[makeQuery(id+"F20.opExtrude","CAP_EDGE",EDGE,{"disambiguationData":[OSD([subQ0])],"isStart":false}),makeQuery(id+"F23.opExtrude","SWEPT_EDGE",EDGE,{"disambiguationData":[OSD([subQ1,subQ0]),TDD([makeQuery(id+"F20.opExtrude","CAP_VERTEX",VERTEX,{"disambiguationData":[OSD([subQ1,subQ0])],"isStart":false})])]})]})])]})]})])],"isStart":false})});}
            var Q1;
            {var subQ0=sQuery(id+"F19.wireOp",EDGE,"E23.right");var subQ1=sQuery(id+"F19.wireOp",EDGE,"E23.top");var subQ4=sQuery(id+"F0.wireOp",EDGE,"E5");var subQ5=sQuery(id+"F0.wireOp",EDGE,"E1");var subQ6=sQuery(id+"F0.wireOp",EDGE,"E0");var subQ7=makeQuery(id+"F1.opExtrude","CAP_FACE",FACE,{"disambiguationData":[OSD([subQ6,subQ5,subQ4])],"isStart":false});var subQ8=makeQuery(id+"F1.opExtrude","SWEPT_FACE",FACE,{"disambiguationData":[OSD([subQ6])]});var subQ10=makeQuery(id+"F1.opExtrude","CAP_EDGE",EDGE,{"disambiguationData":[OSD([subQ6])],"isStart":false});Q1=makeQuery(id+"F32.boolean.opBoolean","COPY",EDGE,{"derivedFrom":makeQuery(id+"F32.opExtrude","CAP_EDGE",EDGE,{"disambiguationData":[OSD([subQ6,subQ1,subQ0]),TDD([makeQuery(id+"F27.boolean.opBoolean","INTERSECT",EDGE,{"disambiguationData":[OD(0.0)],"derivedFrom":[makeQuery(id+"F14.boolean.opBoolean","MERGE",FACE,{"derivedFrom":[subQ8,makeQuery(id+"F14.opExtrude","SWEPT_FACE",FACE,{"disambiguationData":[OSD([subQ6]),TDD([makeQuery(id+"F6.boolean.opBoolean","SPLIT",EDGE,{"disambiguationData":[topologyDisambiguationEdgeConnected([subQ8,subQ7]),TD([makeQuery(id+"F1.opExtrude","SWEPT_FACE",FACE,{"disambiguationData":[OSD([subQ4]),TDD([makeQuery(id+"F0.imprint","IMPRINT",EDGE,{"disambiguationData":[TD([[makeQuery(id+"F0.imprint","INTERSECT",VERTEX,{"disambiguationData":[OD(0.0)],"derivedFrom":[subQ5,subQ4]}),1.0]])],"derivedFrom":subQ4})])]})])],"derivedFrom":subQ10})])]}),makeQuery(id+"F14.opExtrude","SWEPT_FACE",FACE,{"disambiguationData":[OSD([subQ6]),TDD([makeQuery(id+"F6.boolean.opBoolean","SPLIT",EDGE,{"disambiguationData":[topologyDisambiguationEdgeConnected([subQ8,subQ7]),TD([makeQuery(id+"F1.opExtrude","SWEPT_FACE",FACE,{"disambiguationData":[OSD([subQ4]),TDD([makeQuery(id+"F0.imprint","IMPRINT",EDGE,{"disambiguationData":[TD([[makeQuery(id+"F0.imprint","INTERSECT",VERTEX,{"disambiguationData":[OD(1.0)],"derivedFrom":[subQ5,subQ4]}),-1.0]])],"derivedFrom":subQ4})])]})])],"derivedFrom":subQ10})])]})]}),makeQuery(id+"F27.opExtrude","SWEPT_FACE",FACE,{"disambiguationData":[OSD([subQ1,subQ0]),TDD([makeQuery(id+"F23.boolean.opBoolean","MERGE",EDGE,{"derivedFrom":[makeQuery(id+"F20.opExtrude","CAP_EDGE",EDGE,{"disambiguationData":[OSD([subQ0])],"isStart":false}),makeQuery(id+"F23.opExtrude","SWEPT_EDGE",EDGE,{"disambiguationData":[OSD([subQ1,subQ0]),TDD([makeQuery(id+"F20.opExtrude","CAP_VERTEX",VERTEX,{"disambiguationData":[OSD([subQ1,subQ0])],"isStart":false})])]})]})])]})]})])],"isStart":false})});}
            fillet(context, id + "F33", {"entities" : qUnion([Q0, Q1]), "radius" : 8 * mm, "tangentPropagation" : true, "allowEdgeOverflow" : false});
        }
    });
